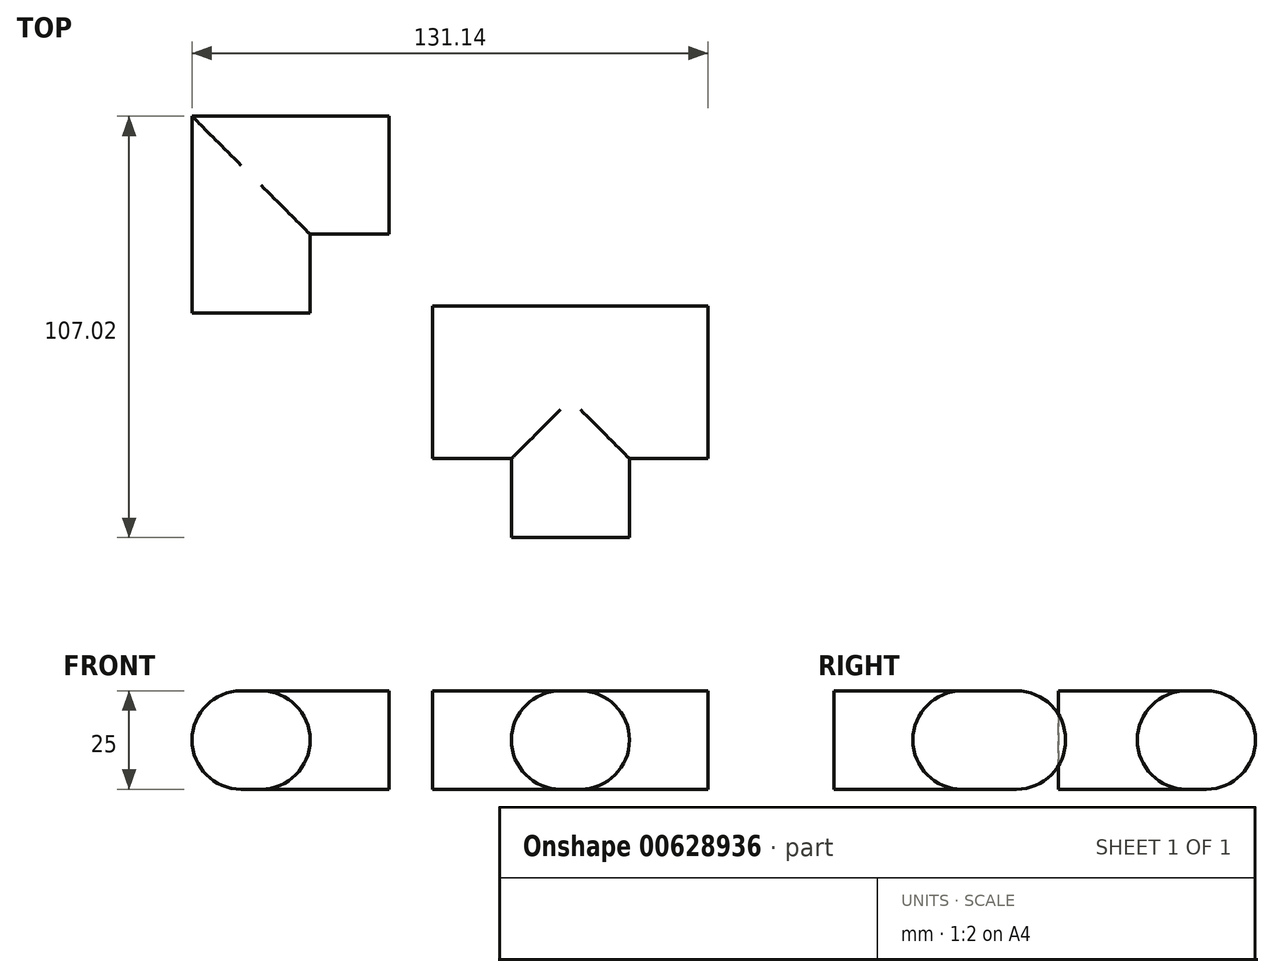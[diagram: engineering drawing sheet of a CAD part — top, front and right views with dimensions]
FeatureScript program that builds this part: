
annotation { "Feature Type Name" : "Feature", "Feature Type Description" : "" }
export const myFeature = defineFeature(function(context is Context, id is Id, definition is map)
    precondition{}
    {
        {
            var Q0;
            Q0=qCreatedBy(makeId("Top.planeOp"),FACE);
            var sketch = newSketch(context, id + "F0", { "sketchPlane" : qUnion([Q0])});
            skLineSegment(sketch, "E0", {"start": v(-65.17, 76.82) * mm, "end": v(-65.17, 36.82) * mm});
            skLineSegment(sketch, "E1", {"start": v(-65.17, 36.82) * mm, "end": v(-45.17, 36.82) * mm});
            skLineSegment(sketch, "E2", {"start": v(-45.17, 36.82) * mm, "end": v(-45.17, 56.82) * mm});
            skLineSegment(sketch, "E3", {"start": v(-45.17, 56.82) * mm, "end": v(-25.17, 56.82) * mm});
            skLineSegment(sketch, "E4", {"start": v(-25.17, 56.82) * mm, "end": v(-25.17, 76.82) * mm});
            skLineSegment(sketch, "E5", {"start": v(-25.17, 76.82) * mm, "end": v(-65.17, 76.82) * mm});
            skLineSegment(sketch, "E6", {"start": v(25.97, -20.2) * mm, "end": v(35.97, -20.2) * mm});
            skLineSegment(sketch, "E7", {"start": v(35.97, -20.2) * mm, "end": v(35.97, -0.2) * mm});
            skLineSegment(sketch, "E8", {"start": v(35.97, -0.2) * mm, "end": v(55.97, -0.2) * mm});
            skLineSegment(sketch, "E9", {"start": v(55.97, -0.2) * mm, "end": v(55.97, 28.6) * mm});
            skLineSegment(sketch, "E10", {"start": v(55.97, 28.6) * mm, "end": v(25.97, 28.6) * mm});
            skLineSegment(sketch, "E11", {"start": v(25.97, -20.2) * mm, "end": v(25.97, 28.6) * mm});
            skPoint(sketch, "E12.start.orphan", {"position": v(15.97, 28.6) * mm});
            skPoint(sketch, "E13.orphan", {"position": v(15.97, -20.2) * mm});
            skLineSegment(sketch, "E14.MirrorCS", {"start": v(-4.03, 28.6) * mm, "end": v(25.97, 28.6) * mm});
            skLineSegment(sketch, "E15.MirrorCS", {"start": v(-4.03, -0.2) * mm, "end": v(-4.03, 28.6) * mm});
            skLineSegment(sketch, "E16.MirrorCS", {"start": v(15.97, -0.2) * mm, "end": v(-4.03, -0.2) * mm});
            skLineSegment(sketch, "E17.MirrorCS", {"start": v(15.97, -20.2) * mm, "end": v(15.97, -0.2) * mm});
            skLineSegment(sketch, "E18.MirrorCS", {"start": v(25.97, -20.2) * mm, "end": v(15.97, -20.2) * mm});
            skLineSegment(sketch, "E19.0", {"start": v(-20.17, 51.82) * mm, "end": v(-20.17, 81.82) * mm});
            skLineSegment(sketch, "E19.1", {"start": v(-70.17, 81.82) * mm, "end": v(-70.17, 31.82) * mm});
            skLineSegment(sketch, "E19.2", {"start": v(-70.17, 31.82) * mm, "end": v(-40.17, 31.82) * mm});
            skLineSegment(sketch, "E19.3", {"start": v(-20.17, 81.82) * mm, "end": v(-70.17, 81.82) * mm});
            skLineSegment(sketch, "E19.4", {"start": v(-40.17, 31.82) * mm, "end": v(-40.17, 51.82) * mm});
            skLineSegment(sketch, "E19.5", {"start": v(-40.17, 51.82) * mm, "end": v(-20.17, 51.82) * mm});
            skLineSegment(sketch, "E20.0", {"start": v(60.97, -5.2) * mm, "end": v(60.97, 33.6) * mm});
            skLineSegment(sketch, "E20.1", {"start": v(40.97, -5.2) * mm, "end": v(60.97, -5.2) * mm});
            skLineSegment(sketch, "E20.2", {"start": v(60.97, 33.6) * mm, "end": v(25.97, 33.6) * mm});
            skLineSegment(sketch, "E20.3", {"start": v(40.97, -25.2) * mm, "end": v(40.97, -5.2) * mm});
            skLineSegment(sketch, "E20.4", {"start": v(25.97, -25.2) * mm, "end": v(40.97, -25.2) * mm});
            skLineSegment(sketch, "E20.5", {"start": v(25.97, -25.2) * mm, "end": v(10.97, -25.2) * mm});
            skLineSegment(sketch, "E20.6", {"start": v(-9.03, 33.6) * mm, "end": v(25.97, 33.6) * mm});
            skLineSegment(sketch, "E20.7", {"start": v(-9.03, -5.2) * mm, "end": v(-9.03, 33.6) * mm});
            skLineSegment(sketch, "E20.8", {"start": v(10.97, -5.2) * mm, "end": v(-9.03, -5.2) * mm});
            skLineSegment(sketch, "E20.9", {"start": v(10.97, -25.2) * mm, "end": v(10.97, -5.2) * mm});
            skSolve(sketch);
        }
        {
            var Q0;
            Q0=makeQuery(id+"F0.imprint","IMPRINT",FACE,{"disambiguationData":[TD([[makeQuery(id+"F0.imprint","IMPRINT",EDGE,{"derivedFrom":sQuery(id+"F0.wireOp",EDGE,"E11")}),1.0]])]});
            var Q1;
            Q1=makeQuery(id+"F0.imprint","IMPRINT",FACE,{"disambiguationData":[TD([[makeQuery(id+"F0.imprint","IMPRINT",EDGE,{"derivedFrom":sQuery(id+"F0.wireOp",EDGE,"E6")}),1.0]])]});
            var Q2;
            Q2=makeQuery(id+"F0.imprint","IMPRINT",FACE,{"disambiguationData":[TD([[makeQuery(id+"F0.imprint","IMPRINT",EDGE,{"derivedFrom":sQuery(id+"F0.wireOp",EDGE,"E6")}),-1.0]])]});
            var Q3;
            Q3=makeQuery(id+"F0.imprint","IMPRINT",FACE,{"disambiguationData":[TD([[makeQuery(id+"F0.imprint","IMPRINT",EDGE,{"derivedFrom":sQuery(id+"F0.wireOp",EDGE,"E0")}),-1.0]])]});
            var Q4;
            Q4=makeQuery(id+"F0.imprint","IMPRINT",FACE,{"disambiguationData":[TD([[makeQuery(id+"F0.imprint","IMPRINT",EDGE,{"derivedFrom":sQuery(id+"F0.wireOp",EDGE,"E0")}),1.0]])]});
            extrude(context, id + "F1", {"entities" : qUnion([Q0, Q1, Q2, Q3, Q4]), "depth" : 25 * mm, "offsetDistance" : 25 * mm});
        }
        {
            var Q0;
            Q0=makeQuery(id+"F1.opExtrude","CAP_EDGE",EDGE,{"disambiguationData":[OSD([sQuery(id+"F0.wireOp",EDGE,"E19.3")])],"isStart":false});
            var Q1;
            Q1=makeQuery(id+"F1.opExtrude","CAP_EDGE",EDGE,{"disambiguationData":[OSD([sQuery(id+"F0.wireOp",EDGE,"E19.1")])],"isStart":false});
            var Q2;
            Q2=makeQuery(id+"F1.opExtrude","CAP_EDGE",EDGE,{"disambiguationData":[OSD([sQuery(id+"F0.wireOp",EDGE,"E19.4")])],"isStart":false});
            var Q3;
            Q3=makeQuery(id+"F1.opExtrude","CAP_EDGE",EDGE,{"disambiguationData":[OSD([sQuery(id+"F0.wireOp",EDGE,"E19.5")])],"isStart":false});
            var Q4;
            Q4=makeQuery(id+"F1.opExtrude","CAP_EDGE",EDGE,{"disambiguationData":[OSD([sQuery(id+"F0.wireOp",EDGE,"E19.1")])],"isStart":true});
            var Q5;
            Q5=makeQuery(id+"F1.opExtrude","CAP_EDGE",EDGE,{"disambiguationData":[OSD([sQuery(id+"F0.wireOp",EDGE,"E19.3")])],"isStart":true});
            var Q6;
            Q6=makeQuery(id+"F1.opExtrude","CAP_EDGE",EDGE,{"disambiguationData":[OSD([sQuery(id+"F0.wireOp",EDGE,"E19.5")])],"isStart":true});
            var Q7;
            Q7=makeQuery(id+"F1.opExtrude","CAP_EDGE",EDGE,{"disambiguationData":[OSD([sQuery(id+"F0.wireOp",EDGE,"E19.4")])],"isStart":true});
            var Q8;
            Q8=makeQuery(id+"F1.opExtrude","CAP_EDGE",EDGE,{"disambiguationData":[OSD([sQuery(id+"F0.wireOp",EDGE,"E20.8")])],"isStart":false});
            var Q9;
            Q9=makeQuery(id+"F1.opExtrude","CAP_EDGE",EDGE,{"disambiguationData":[OSD([sQuery(id+"F0.wireOp",EDGE,"E20.9")])],"isStart":false});
            var Q10;
            Q10=makeQuery(id+"F1.opExtrude","CAP_EDGE",EDGE,{"disambiguationData":[OSD([sQuery(id+"F0.wireOp",EDGE,"E20.3")])],"isStart":false});
            var Q11;
            Q11=makeQuery(id+"F1.opExtrude","CAP_EDGE",EDGE,{"disambiguationData":[OSD([sQuery(id+"F0.wireOp",EDGE,"E20.1")])],"isStart":false});
            var Q12;
            Q12=makeQuery(id+"F1.opExtrude","CAP_EDGE",EDGE,{"disambiguationData":[OSD([sQuery(id+"F0.wireOp",EDGE,"E20.2"),sQuery(id+"F0.wireOp",EDGE,"E20.6")])],"isStart":false});
            var Q13;
            Q13=makeQuery(id+"F1.opExtrude","CAP_EDGE",EDGE,{"disambiguationData":[OSD([sQuery(id+"F0.wireOp",EDGE,"E20.1")])],"isStart":true});
            var Q14;
            Q14=makeQuery(id+"F1.opExtrude","CAP_EDGE",EDGE,{"disambiguationData":[OSD([sQuery(id+"F0.wireOp",EDGE,"E20.3")])],"isStart":true});
            var Q15;
            Q15=makeQuery(id+"F1.opExtrude","CAP_EDGE",EDGE,{"disambiguationData":[OSD([sQuery(id+"F0.wireOp",EDGE,"E20.9")])],"isStart":true});
            var Q16;
            Q16=makeQuery(id+"F1.opExtrude","CAP_EDGE",EDGE,{"disambiguationData":[OSD([sQuery(id+"F0.wireOp",EDGE,"E20.8")])],"isStart":true});
            var Q17;
            Q17=makeQuery(id+"F1.opExtrude","CAP_EDGE",EDGE,{"disambiguationData":[OSD([sQuery(id+"F0.wireOp",EDGE,"E20.2"),sQuery(id+"F0.wireOp",EDGE,"E20.6")])],"isStart":true});
            fillet(context, id + "F2", {"entities" : qUnion([Q0, Q1, Q2, Q3, Q4, Q5, Q6, Q7, Q8, Q9, Q10, Q11, Q12, Q13, Q14, Q15, Q16, Q17]), "radius" : 12.5 * mm, "tangentPropagation" : true, "allowEdgeOverflow" : false});
        }
    });
